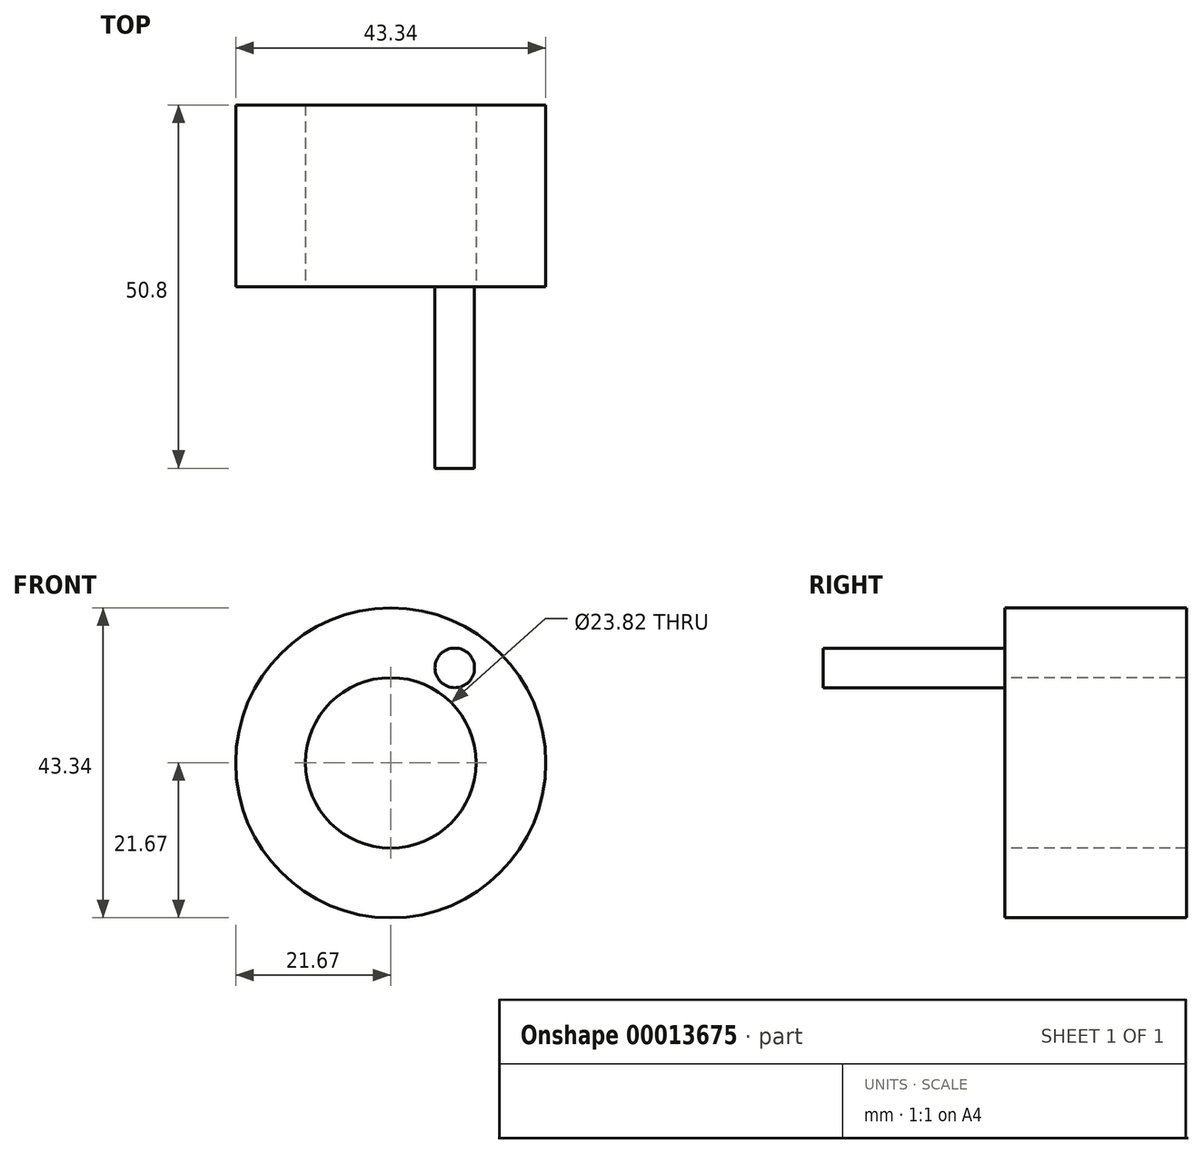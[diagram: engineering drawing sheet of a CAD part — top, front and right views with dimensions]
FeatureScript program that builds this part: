
annotation { "Feature Type Name" : "Feature", "Feature Type Description" : "" }
export const myFeature = defineFeature(function(context is Context, id is Id, definition is map)
    precondition{}
    {
        {
            var Q0;
            Q0=qCreatedBy(makeId("Front.planeOp"),FACE);
            var sketch = newSketch(context, id + "F0", { "sketchPlane" : qUnion([Q0])});
            skCircle(sketch, "E0", {"center": v(0, 0) * mm, "radius": 21.67 * mm});
            skSolve(sketch);
        }
        {
            var Q0;
            Q0=makeQuery(id+"F0.imprint","IMPRINT",FACE,{"disambiguationData":[TD([[makeQuery(id+"F0.imprint","IMPRINT",EDGE,{"derivedFrom":sQuery(id+"F0.wireOp",EDGE,"E0")}),1.0]])]});
            extrude(context, id + "F1", {"entities" : qUnion([Q0]), "oppositeDirection" : true, "depth" : 25.4 * mm});
        }
        {
            var Q0;
            Q0=makeQuery(id+"F1.opExtrude","CAP_FACE",FACE,{"disambiguationData":[OSD([sQuery(id+"F0.wireOp",EDGE,"E0")])],"isStart":true});
            var sketch = newSketch(context, id + "F2", { "sketchPlane" : qUnion([Q0])});
            skCircle(sketch, "E1", {"center": v(0, 0) * mm, "radius": 11.91 * mm});
            skSolve(sketch);
        }
        {
            var Q0;
            Q0 = qSketchRegion(id + "F2", true);
            extrude(context, id + "F3", {"entities" : qUnion([Q0]), "operationType" : NewBodyOperationType.REMOVE, "oppositeDirection" : true, "depth" : 58.53 * mm});
        }
        {
            var Q0;
            Q0=makeQuery(id+"F1.opExtrude","CAP_FACE",FACE,{"disambiguationData":[OSD([sQuery(id+"F0.wireOp",EDGE,"E0")])],"isStart":true});
            var sketch = newSketch(context, id + "F4", { "sketchPlane" : qUnion([Q0])});
            skCircle(sketch, "E2", {"center": v(8.95, 13.27) * mm, "radius": 2.77 * mm});
            skSolve(sketch);
        }
        {
            var Q0;
            Q0 = qSketchRegion(id + "F4", true);
            extrude(context, id + "F5", {"entities" : qUnion([Q0]), "operationType" : NewBodyOperationType.ADD, "depth" : 25.4 * mm});
        }
    });
